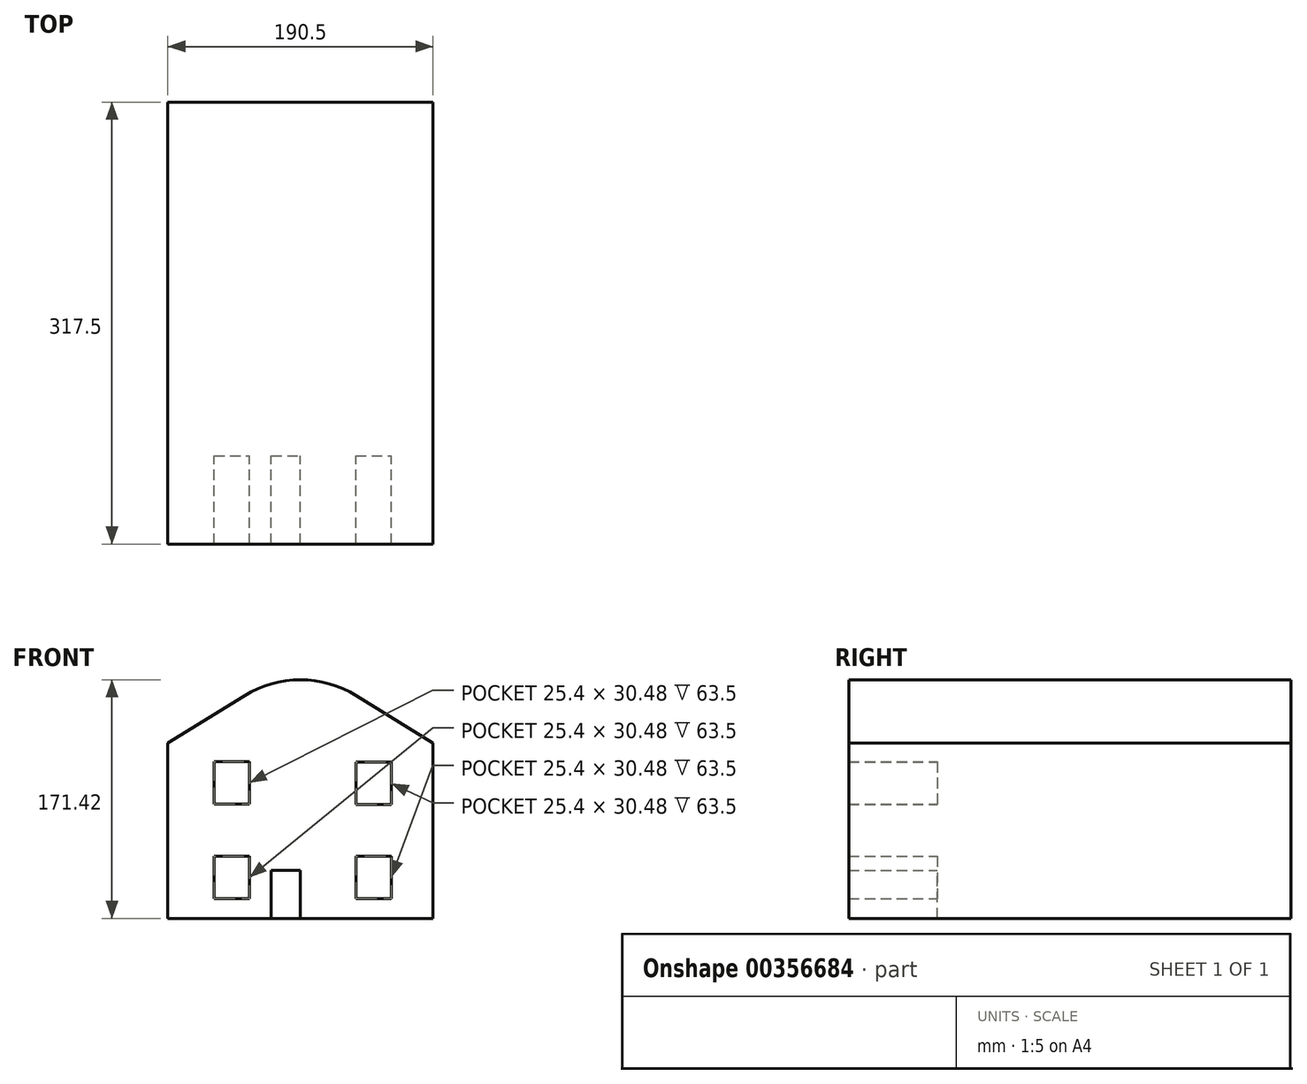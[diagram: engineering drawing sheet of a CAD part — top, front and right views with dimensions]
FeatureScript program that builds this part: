
annotation { "Feature Type Name" : "Feature", "Feature Type Description" : "" }
export const myFeature = defineFeature(function(context is Context, id is Id, definition is map)
    precondition{}
    {
        {
            var Q0;
            Q0=qCreatedBy(makeId("Front.planeOp"),FACE);
            var sketch = newSketch(context, id + "F0", { "sketchPlane" : qUnion([Q0])});
            skLineSegment(sketch, "E0.bottom", {"start": v(-95.25, 62.95) * mm, "end": v(95.25, 62.95) * mm});
            skLineSegment(sketch, "E0.top", {"start": v(-95.25, -62.95) * mm, "end": v(95.25, -62.95) * mm});
            skLineSegment(sketch, "E0.left", {"start": v(-95.25, 62.95) * mm, "end": v(-95.25, -62.95) * mm});
            skLineSegment(sketch, "E0.right", {"start": v(95.25, 62.95) * mm, "end": v(95.25, -62.95) * mm});
            skPoint(sketch, "E0.middle", {"position": v(0, 0) * mm});
            skLineSegment(sketch, "E1", {"start": v(-95.25, 62.95) * mm, "end": v(0, 121.87) * mm});
            skLineSegment(sketch, "E2", {"start": v(0, 121.87) * mm, "end": v(95.25, 62.95) * mm});
            skLineSegment(sketch, "E3.bottom", {"start": v(-62.02, 49.7) * mm, "end": v(-36.62, 49.7) * mm});
            skLineSegment(sketch, "E3.top", {"start": v(-62.02, 19.23) * mm, "end": v(-36.62, 19.23) * mm});
            skLineSegment(sketch, "E3.left", {"start": v(-62.02, 49.7) * mm, "end": v(-62.02, 19.23) * mm});
            skLineSegment(sketch, "E3.right", {"start": v(-36.62, 49.7) * mm, "end": v(-36.62, 19.23) * mm});
            skPoint(sketch, "E3.middle", {"position": v(-49.32, 34.47) * mm});
            skLineSegment(sketch, "E4.bottom", {"start": v(-20.88, -62.95) * mm, "end": v(0, -62.95) * mm});
            skLineSegment(sketch, "E4.top", {"start": v(-20.88, -28.4) * mm, "end": v(0, -28.4) * mm});
            skLineSegment(sketch, "E4.left", {"start": v(-20.88, -62.95) * mm, "end": v(-20.88, -28.4) * mm});
            skLineSegment(sketch, "E4.right", {"start": v(0, -62.95) * mm, "end": v(0, -28.4) * mm});
            skLineSegment(sketch, "E5.bottom", {"start": v(-62.02, -18.44) * mm, "end": v(-36.62, -18.44) * mm});
            skLineSegment(sketch, "E5.top", {"start": v(-62.02, -48.92) * mm, "end": v(-36.62, -48.92) * mm});
            skLineSegment(sketch, "E5.left", {"start": v(-62.02, -18.44) * mm, "end": v(-62.02, -48.92) * mm});
            skLineSegment(sketch, "E5.right", {"start": v(-36.62, -18.44) * mm, "end": v(-36.62, -48.92) * mm});
            skPoint(sketch, "E5.middle", {"position": v(-49.32, -33.68) * mm});
            skLineSegment(sketch, "E6.bottom", {"start": v(247.99, 77.35) * mm, "end": v(251.86, 77.35) * mm});
            skLineSegment(sketch, "E6.top", {"start": v(247.99, 69.41) * mm, "end": v(251.86, 69.41) * mm});
            skLineSegment(sketch, "E6.left", {"start": v(247.99, 77.35) * mm, "end": v(247.99, 69.41) * mm});
            skLineSegment(sketch, "E6.right", {"start": v(251.86, 77.35) * mm, "end": v(251.86, 69.41) * mm});
            skPoint(sketch, "E6.middle", {"position": v(249.92, 73.38) * mm});
            skLineSegment(sketch, "E7.bottom", {"start": v(39.82, -18.44) * mm, "end": v(65.22, -18.44) * mm});
            skLineSegment(sketch, "E7.top", {"start": v(39.82, -48.92) * mm, "end": v(65.22, -48.92) * mm});
            skLineSegment(sketch, "E7.left", {"start": v(39.82, -18.44) * mm, "end": v(39.82, -48.92) * mm});
            skLineSegment(sketch, "E7.right", {"start": v(65.22, -18.44) * mm, "end": v(65.22, -48.92) * mm});
            skPoint(sketch, "E7.middle", {"position": v(52.52, -33.68) * mm});
            skLineSegment(sketch, "E8.bottom", {"start": v(39.82, 49.27) * mm, "end": v(65.22, 49.27) * mm});
            skLineSegment(sketch, "E8.top", {"start": v(39.82, 18.8) * mm, "end": v(65.22, 18.8) * mm});
            skLineSegment(sketch, "E8.left", {"start": v(39.82, 49.27) * mm, "end": v(39.82, 18.8) * mm});
            skLineSegment(sketch, "E8.right", {"start": v(65.22, 49.27) * mm, "end": v(65.22, 18.8) * mm});
            skPoint(sketch, "E8.middle", {"position": v(52.52, 34.03) * mm});
            skPoint(sketch, "E9", {"position": v(-49.32, 19.23) * mm});
            skPoint(sketch, "E10", {"position": v(-36.62, -33.68) * mm});
            skPoint(sketch, "E11", {"position": v(52.52, -18.44) * mm});
            skSolve(sketch);
        }
        {
            var Q0;
            Q0=makeQuery(id+"F0.imprint","IMPRINT",FACE,{"disambiguationData":[TD([[makeQuery(id+"F0.imprint","IMPRINT",EDGE,{"derivedFrom":sQuery(id+"F0.wireOp",EDGE,"E0.bottom")}),1.0]])]});
            var Q1;
            Q1=makeQuery(id+"F0.imprint","IMPRINT",FACE,{"disambiguationData":[TD([[makeQuery(id+"F0.imprint","IMPRINT",EDGE,{"derivedFrom":sQuery(id+"F0.wireOp",EDGE,"E0.bottom")}),-1.0]])]});
            var Q2;
            Q2=sQuery(id+"F0.wireOp",EDGE,"E0.top");
            var Q3;
            Q3=sQuery(id+"F0.wireOp",EDGE,"E0.left");
            var Q4;
            Q4=sQuery(id+"F0.wireOp",EDGE,"E1");
            var Q5;
            Q5=sQuery(id+"F0.wireOp",EDGE,"E0.bottom");
            var Q6;
            Q6=sQuery(id+"F0.wireOp",EDGE,"E2");
            var Q7;
            Q7=sQuery(id+"F0.wireOp",EDGE,"E0.right");
            extrude(context, id + "F1", {"entities" : qUnion([Q0, Q1]), "surfaceEntities" : qUnion([Q2, Q3, Q4, Q5, Q6, Q7]), "depth" : 317.5 * mm});
        }
        {
            var Q0;
            Q0=makeQuery(id+"F0.imprint","IMPRINT",FACE,{"disambiguationData":[TD([[makeQuery(id+"F0.imprint","IMPRINT",EDGE,{"derivedFrom":sQuery(id+"F0.wireOp",EDGE,"E8.bottom")}),-1.0]])]});
            var Q1;
            Q1=makeQuery(id+"F0.imprint","IMPRINT",FACE,{"disambiguationData":[TD([[makeQuery(id+"F0.imprint","IMPRINT",EDGE,{"derivedFrom":sQuery(id+"F0.wireOp",EDGE,"E3.bottom")}),-1.0]])]});
            var Q2;
            Q2=makeQuery(id+"F0.imprint","IMPRINT",FACE,{"disambiguationData":[TD([[makeQuery(id+"F0.imprint","IMPRINT",EDGE,{"derivedFrom":sQuery(id+"F0.wireOp",EDGE,"E7.bottom")}),-1.0]])]});
            var Q3;
            Q3=makeQuery(id+"F0.imprint","IMPRINT",FACE,{"disambiguationData":[TD([[makeQuery(id+"F0.imprint","IMPRINT",EDGE,{"derivedFrom":sQuery(id+"F0.wireOp",EDGE,"E5.bottom")}),-1.0]])]});
            var Q4;
            Q4=makeQuery(id+"F0.imprint","IMPRINT",FACE,{"disambiguationData":[TD([[makeQuery(id+"F0.imprint","IMPRINT",EDGE,{"derivedFrom":sQuery(id+"F0.wireOp",EDGE,"E4.bottom")}),1.0]])]});
            var Q5;
            Q5=makeQuery(id+"F0.imprint","IMPRINT",FACE,{"disambiguationData":[TD([[makeQuery(id+"F0.imprint","IMPRINT",EDGE,{"derivedFrom":sQuery(id+"F0.wireOp",EDGE,"E4.top")}),-1.0]])]});
            extrude(context, id + "F2", {"entities" : qUnion([Q0, Q1, Q2, Q3, Q4, Q5]), "operationType" : NewBodyOperationType.ADD, "depth" : 254 * mm});
        }
        {
            var Q0;
            Q0=makeQuery(id+"F1.opExtrude","SWEPT_EDGE",EDGE,{"disambiguationData":[OSD([sQuery(id+"F0.wireOp",EDGE,"E1"),sQuery(id+"F0.wireOp",EDGE,"E2")])]});
            fillet(context, id + "F3", {"entities" : qUnion([Q0]), "radius" : 76.2 * mm, "tangentPropagation" : true, "allowEdgeOverflow" : false});
        }
    });
